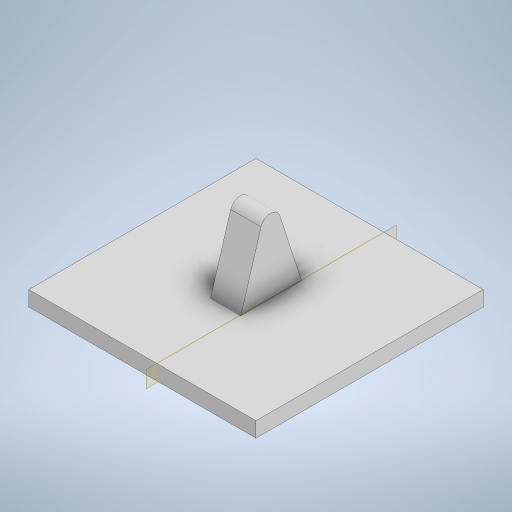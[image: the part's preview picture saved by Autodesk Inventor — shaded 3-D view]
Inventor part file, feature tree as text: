
AUTODESK INVENTOR PART (.ipt)
format: ipt  version: 2023 (Build 270158000, 158)  size: 222,208 bytes
history: native  units: mm
features: extrude x2, sketch x2, plane x1
ambient origin geometry x8: Origin, YZ Plane, XZ Plane, XY Plane, X Axis, Y Axis, Z Axis, Center Point
bodies: Solid1 (feature_tree)
feature tree (5):
  extrude  "Extrusion1"  Depth=30.0mm
  plane  "Work Plane1"
  extrude  "Extrusion2"  [1 undecoded]
  sketch  "Sketch1"  dims[d0=30.0mm d1=30.0mm]
  sketch  "Sketch2"  dims[d2=2.0mm d3=0.0mm d4=-13.0mm d5=11.0mm d6=8.0mm d7=4.0mm d8=0.0mm]
note: 1 required parameter value undecoded (feature->parameter linkage not recoverable at this tier; creation-order binding heuristic only, values carry confidence <= 0.55)
